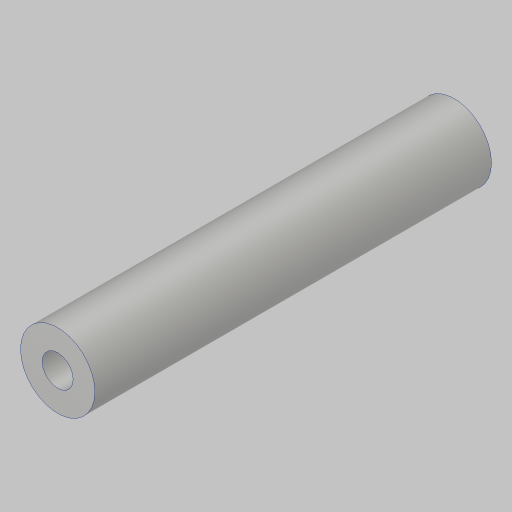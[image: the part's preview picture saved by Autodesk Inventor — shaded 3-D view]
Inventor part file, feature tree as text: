
AUTODESK INVENTOR PART (.ipt)
format: ipt  version: 2023.5 (Build 275446000, 446)  size: 105,984 bytes
history: native  units: in
note: dims shown in document units (in); Inventor stores cm internally (conversion verified against a paired STEP export)
features: extrude x1, hole x1
ambient origin geometry x8: Origin, YZ Plane, XZ Plane, XY Plane, X Axis, Y Axis, Z Axis, Center Point
bodies: Solid1 (feature_tree)
feature tree (2):
  extrude  "Extrusion1"  Depth=2.0in
  hole  "Hole1"  [1 undecoded]
note: 1 required parameter value undecoded (feature->parameter linkage not recoverable at this tier; creation-order binding heuristic only, values carry confidence <= 0.55)
